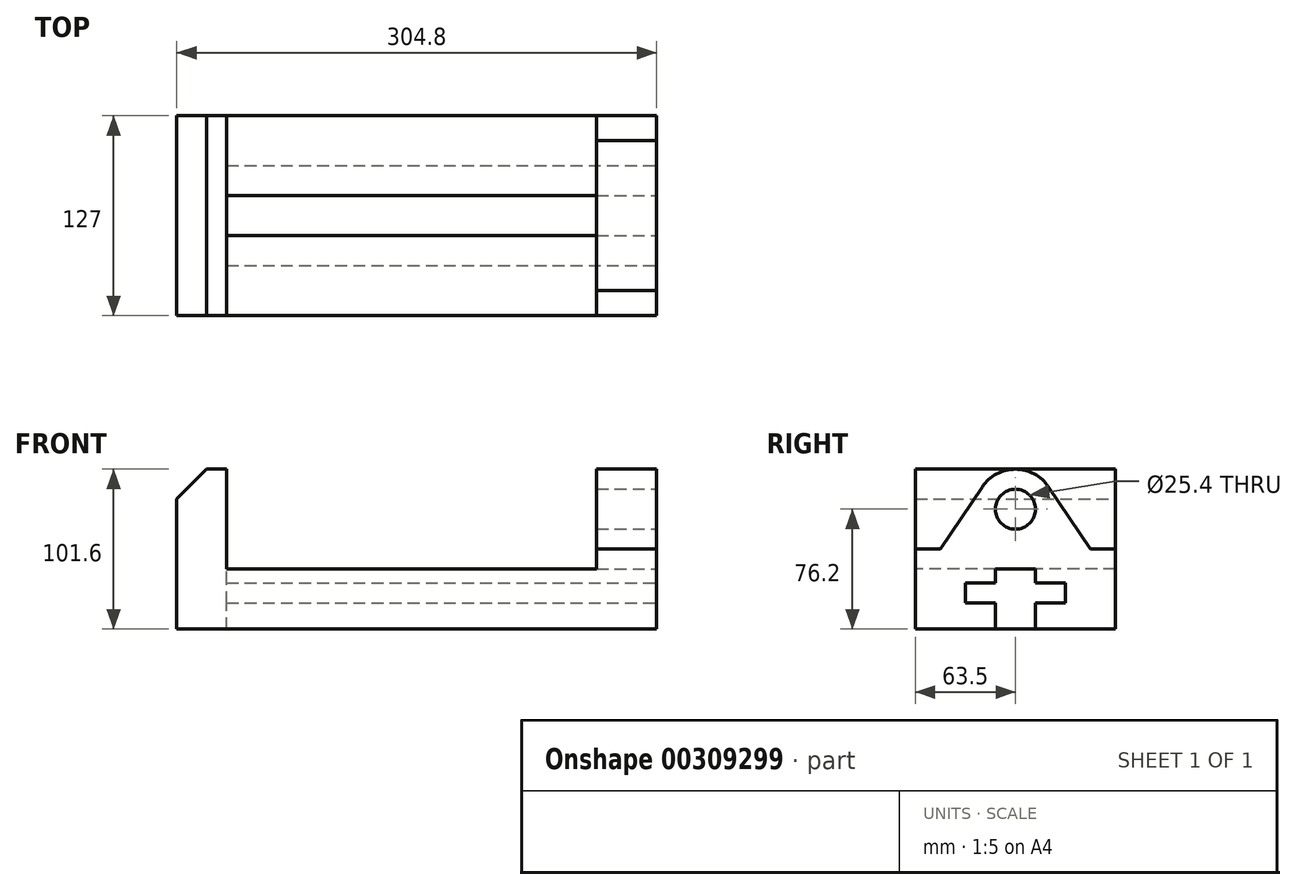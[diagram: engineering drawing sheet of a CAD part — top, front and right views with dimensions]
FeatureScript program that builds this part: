
annotation { "Feature Type Name" : "Feature", "Feature Type Description" : "" }
export const myFeature = defineFeature(function(context is Context, id is Id, definition is map)
    precondition{}
    {
        {
            var Q0;
            Q0=qCreatedBy(makeId("Front.planeOp"),FACE);
            var sketch = newSketch(context, id + "F0", { "sketchPlane" : qUnion([Q0])});
            skLineSegment(sketch, "E0", {"start": v(0, 0) * mm, "end": v(0, 50.8) * mm});
            skLineSegment(sketch, "E1", {"start": v(0, 50.8) * mm, "end": v(304.8, 50.8) * mm});
            skLineSegment(sketch, "E2", {"start": v(304.8, 50.8) * mm, "end": v(304.8, 0) * mm});
            skLineSegment(sketch, "E3", {"start": v(304.8, 0) * mm, "end": v(0, 0) * mm});
            skSolve(sketch);
        }
        {
            var Q0;
            Q0 = qSketchRegion(id + "F0", true);
            extrude(context, id + "F1", {"entities" : qUnion([Q0]), "depth" : 127 * mm});
        }
        {
            var Q0;
            Q0=makeQuery(id+"F1.opExtrude","SWEPT_FACE",FACE,{"disambiguationData":[OSD([sQuery(id+"F0.wireOp",EDGE,"E2")])]});
            var sketch = newSketch(context, id + "F2", { "sketchPlane" : qUnion([Q0])});
            skLineSegment(sketch, "E4", {"start": v(-63.5, 63.22) * mm, "end": v(-63.5, -31.41) * mm, "construction": true});
            skPoint(sketch, "E4.startSnap0", {"position": v(-63.5, 0) * mm});
            skLineSegment(sketch, "E5", {"start": v(-63.5, 0) * mm, "end": v(-76.2, 0) * mm});
            skLineSegment(sketch, "E6", {"start": v(-76.2, 0) * mm, "end": v(-76.2, 16.5) * mm});
            skLineSegment(sketch, "E7", {"start": v(-76.2, 16.5) * mm, "end": v(-95.25, 16.5) * mm});
            skLineSegment(sketch, "E8", {"start": v(-95.25, 16.5) * mm, "end": v(-95.25, 29.2) * mm});
            skLineSegment(sketch, "E9", {"start": v(-95.25, 29.2) * mm, "end": v(-76.2, 29.2) * mm});
            skLineSegment(sketch, "E10", {"start": v(-76.2, 29.2) * mm, "end": v(-76.2, 38.1) * mm});
            skLineSegment(sketch, "E11", {"start": v(-76.2, 38.1) * mm, "end": v(-63.5, 38.1) * mm});
            skLineSegment(sketch, "E12", {"start": v(-63.5, 38.1) * mm, "end": v(-63.5, 0) * mm});
            skLineSegment(sketch, "E13.MirrorCS", {"start": v(-50.8, 29.2) * mm, "end": v(-50.8, 38.1) * mm});
            skLineSegment(sketch, "E14.MirrorCS", {"start": v(-50.8, 38.1) * mm, "end": v(-63.5, 38.1) * mm});
            skLineSegment(sketch, "E15.MirrorCS", {"start": v(-31.75, 29.2) * mm, "end": v(-50.8, 29.2) * mm});
            skLineSegment(sketch, "E16.MirrorCS", {"start": v(-31.75, 16.5) * mm, "end": v(-31.75, 29.2) * mm});
            skLineSegment(sketch, "E17.MirrorCS", {"start": v(-50.8, 16.5) * mm, "end": v(-31.75, 16.5) * mm});
            skLineSegment(sketch, "E18.MirrorCS", {"start": v(-50.8, 0) * mm, "end": v(-50.8, 16.5) * mm});
            skLineSegment(sketch, "E19.MirrorCS", {"start": v(-63.5, 0) * mm, "end": v(-50.8, 0) * mm});
            skSolve(sketch);
        }
        {
            var Q0;
            Q0 = qSketchRegion(id + "F2", true);
            extrude(context, id + "F3", {"entities" : qUnion([Q0]), "operationType" : NewBodyOperationType.REMOVE, "oppositeDirection" : true, "depth" : 273.05 * mm});
        }
        {
            var Q0;
            Q0=makeQuery(id+"F1.opExtrude","CAP_FACE",FACE,{"disambiguationData":[OSD([sQuery(id+"F0.wireOp",EDGE,"E0"),sQuery(id+"F0.wireOp",EDGE,"E1"),sQuery(id+"F0.wireOp",EDGE,"E2"),sQuery(id+"F0.wireOp",EDGE,"E3")])],"isStart":false});
            var sketch = newSketch(context, id + "F4", { "sketchPlane" : qUnion([Q0])});
            skLineSegment(sketch, "E20", {"start": v(266.7, 50.8) * mm, "end": v(266.7, 38.1) * mm});
            skLineSegment(sketch, "E21", {"start": v(266.7, 38.1) * mm, "end": v(0, 38.1) * mm});
            skLineSegment(sketch, "E22", {"start": v(0, 38.1) * mm, "end": v(0, 50.8) * mm});
            skLineSegment(sketch, "E23", {"start": v(0, 50.8) * mm, "end": v(266.7, 50.8) * mm});
            skSolve(sketch);
        }
        {
            var Q0;
            Q0 = qSketchRegion(id + "F4", true);
            extrude(context, id + "F5", {"entities" : qUnion([Q0]), "operationType" : NewBodyOperationType.REMOVE, "endBound" : BoundingType.THROUGH_ALL, "oppositeDirection" : true, "depth" : 25.4 * mm});
        }
        {
            var Q0;
            Q0=qCreatedBy(makeId("Front.planeOp"),FACE);
            var sketch = newSketch(context, id + "F6", { "sketchPlane" : qUnion([Q0])});
            skLineSegment(sketch, "E24", {"start": v(0, 38.1) * mm, "end": v(0, 101.6) * mm});
            skLineSegment(sketch, "E25", {"start": v(0, 101.6) * mm, "end": v(31.75, 101.6) * mm});
            skLineSegment(sketch, "E26", {"start": v(31.75, 101.6) * mm, "end": v(31.75, 38.1) * mm});
            skLineSegment(sketch, "E27", {"start": v(31.75, 38.1) * mm, "end": v(0, 38.1) * mm});
            skSolve(sketch);
        }
        {
            var Q0;
            Q0 = qSketchRegion(id + "F6", true);
            extrude(context, id + "F7", {"entities" : qUnion([Q0]), "operationType" : NewBodyOperationType.ADD, "depth" : 127 * mm});
        }
        {
            var Q0;
            Q0=makeQuery(id+"F1.opExtrude","SWEPT_FACE",FACE,{"disambiguationData":[OSD([sQuery(id+"F0.wireOp",EDGE,"E1")])]});
            var sketch = newSketch(context, id + "F8", { "sketchPlane" : qUnion([Q0])});
            skLineSegment(sketch, "E28", {"start": v(266.7, 0) * mm, "end": v(304.8, 0) * mm});
            skLineSegment(sketch, "E29", {"start": v(304.8, 0) * mm, "end": v(304.8, -127) * mm});
            skLineSegment(sketch, "E30", {"start": v(304.8, -127) * mm, "end": v(266.7, -127) * mm});
            skLineSegment(sketch, "E31", {"start": v(266.7, -127) * mm, "end": v(266.7, 0) * mm});
            skSolve(sketch);
        }
        {
            var Q0;
            Q0 = qSketchRegion(id + "F8", true);
            extrude(context, id + "F9", {"entities" : qUnion([Q0]), "operationType" : NewBodyOperationType.ADD, "depth" : 50.8 * mm});
        }
        {
            var Q0;
            Q0=makeQuery(id+"F9.boolean.opBoolean","MERGE",FACE,{"derivedFrom":[makeQuery(id+"F1.opExtrude","SWEPT_FACE",FACE,{"disambiguationData":[OSD([sQuery(id+"F0.wireOp",EDGE,"E2")])]}),makeQuery(id+"F9.opExtrude","SWEPT_FACE",FACE,{"disambiguationData":[OSD([sQuery(id+"F8.wireOp",EDGE,"E29")])]})]});
            var sketch = newSketch(context, id + "F10", { "sketchPlane" : qUnion([Q0])});
            skLineSegment(sketch, "E32", {"start": v(-127, 50.8) * mm, "end": v(-111.12, 50.8) * mm});
            skLineSegment(sketch, "E33", {"start": v(-111.12, 50.8) * mm, "end": v(-84.6, 90.35) * mm});
            skLineSegment(sketch, "E34", {"start": v(0, 50.8) * mm, "end": v(-15.88, 50.8) * mm});
            skLineSegment(sketch, "E35", {"start": v(-15.88, 50.8) * mm, "end": v(-42.4, 90.35) * mm});
            skArc(sketch, "E36", {"start": v(-42.4, 90.35) * mm, "mid": v(-63.5, 101.6) * mm, "end": v(-84.6, 90.35) * mm});
            skCircle(sketch, "E37", {"center": v(-63.5, 76.2) * mm, "radius": 12.7 * mm});
            skSolve(sketch);
        }
        {
            var Q0;
            Q0=makeQuery(id+"F10.imprint","IMPRINT",FACE,{"disambiguationData":[TD([[makeQuery(id+"F10.imprint","IMPRINT",EDGE,{"derivedFrom":sQuery(id+"F10.wireOp",EDGE,"E37")}),1.0]])]});
            var Q1;
            {var subQ7=sQuery(id+"F10.wireOp",EDGE,"E32");Q1=makeQuery(id+"F10.imprint","IMPRINT",FACE,{"disambiguationData":[TD([[makeQuery(id+"F10.imprint","IMPRINT",EDGE,{"derivedFrom":subQ7}),1.0]])]});}
            var Q2;
            {var subQ7=sQuery(id+"F10.wireOp",EDGE,"E34");Q2=makeQuery(id+"F10.imprint","IMPRINT",FACE,{"disambiguationData":[TD([[makeQuery(id+"F10.imprint","IMPRINT",EDGE,{"derivedFrom":subQ7}),-1.0]])]});}
            extrude(context, id + "F11", {"entities" : qUnion([Q0, Q1, Q2]), "operationType" : NewBodyOperationType.REMOVE, "endBound" : BoundingType.UP_TO_NEXT, "oppositeDirection" : true, "depth" : 25.4 * mm});
        }
        {
            var Q0;
            Q0=makeQuery(id+"F7.opExtrude","SWEPT_EDGE",EDGE,{"disambiguationData":[OSD([sQuery(id+"F6.wireOp",EDGE,"E24"),sQuery(id+"F6.wireOp",EDGE,"E25")])]});
            chamfer(context, id + "F12", {"entities" : qUnion([Q0]), "width" : 19.05 * mm, "tangentPropagation" : true});
        }
    });
